# Revit family: LAMP_MICROSHOT
name_source: partatom
category: Modelos genéricos
revit_build: Autodesk Revit 2015 (Build: 20140606_1530(x64)
units: mm (PartAtom-declared; Revit-internal decimal feet)

## types (4) — shared parameters
Comentarios de tipo = Availability of tilting between -30º and 90º when placed in a project.
Diameter = 94 mm  [stored 0.308399 ft]
Elevación por defecto = 1219 mm
Fabricante = LAMP
Finish = Texturised grey
Gear = Electronic
Height = 296 mm  [stored 0.971129 ft]
IEE = A++
Installation instructions = http://www.lamp.es
Insulation class = III
LED Lifetime = 50.000 L90 B10
Lamp = HIGH POWER LED
Last update = 26/07/2018
Luminaire type = Outdoor - Spotlight
MacAdam = 4
Manufacturer URL = http://www.lamp.es
Manufacturer country = Spain
Manufacturer name = LAMP
Model explanation = Availability of tilting between -30º and 90º when placed in a project.
Plum = 9 W
Power = 6 W
Power Supply = 700mA DC
Product URL = http://www.lamp.es
Product datasheet = http://www.lamp.es
Protection rating = IP65 / IK06
Type = HI POWER CREE
Weight = 0.70 kg

## per-type parameters (varying)
| type | CRI | Descripción | Efficacy | Initial color | Initial intensity | Modelo | Photometric web file | Product code |
| 369LM 3000 MEDIUM FLOOD | 80 | MICRO SHOT LED 600 WW MFL GR. | 42 lm/W | 3000 K | 369 lm | 7541073 | Cabeza Microshot : 369LM 3000 MEDIUM FLOOD | 7541073 |
| 414LM 3000 SPOT | 80 | MICRO SHOT LED 600 WW SP GR. | 47 lm/W | 3000 K | 414 lm | 7541053 | Cabeza Microshot : 414LM 3000 SPOT | 7541053 |
| 421LM 4000 MEDIUM FLOOD | 75 | MICRO SHOT LED 600 NW MFL GR. | 48 lm/W | 4000 K | 421 lm | 7541063 | Cabeza Microshot : 421LM 4000 MEDIUM FLOOD | 7541063 |
| 472LM 4000 SPOT | 75 | MICRO SHOT LED 600 NW SP GR. | 54 lm/W | 4000 K | 472 lm | 7541043 | Cabeza Microshot : 472LM 4000 SPOT | 7541043 |

note: [stored X ft] marks values corroborated as IEEE doubles in the binary element streams (Revit-internal decimal feet)
